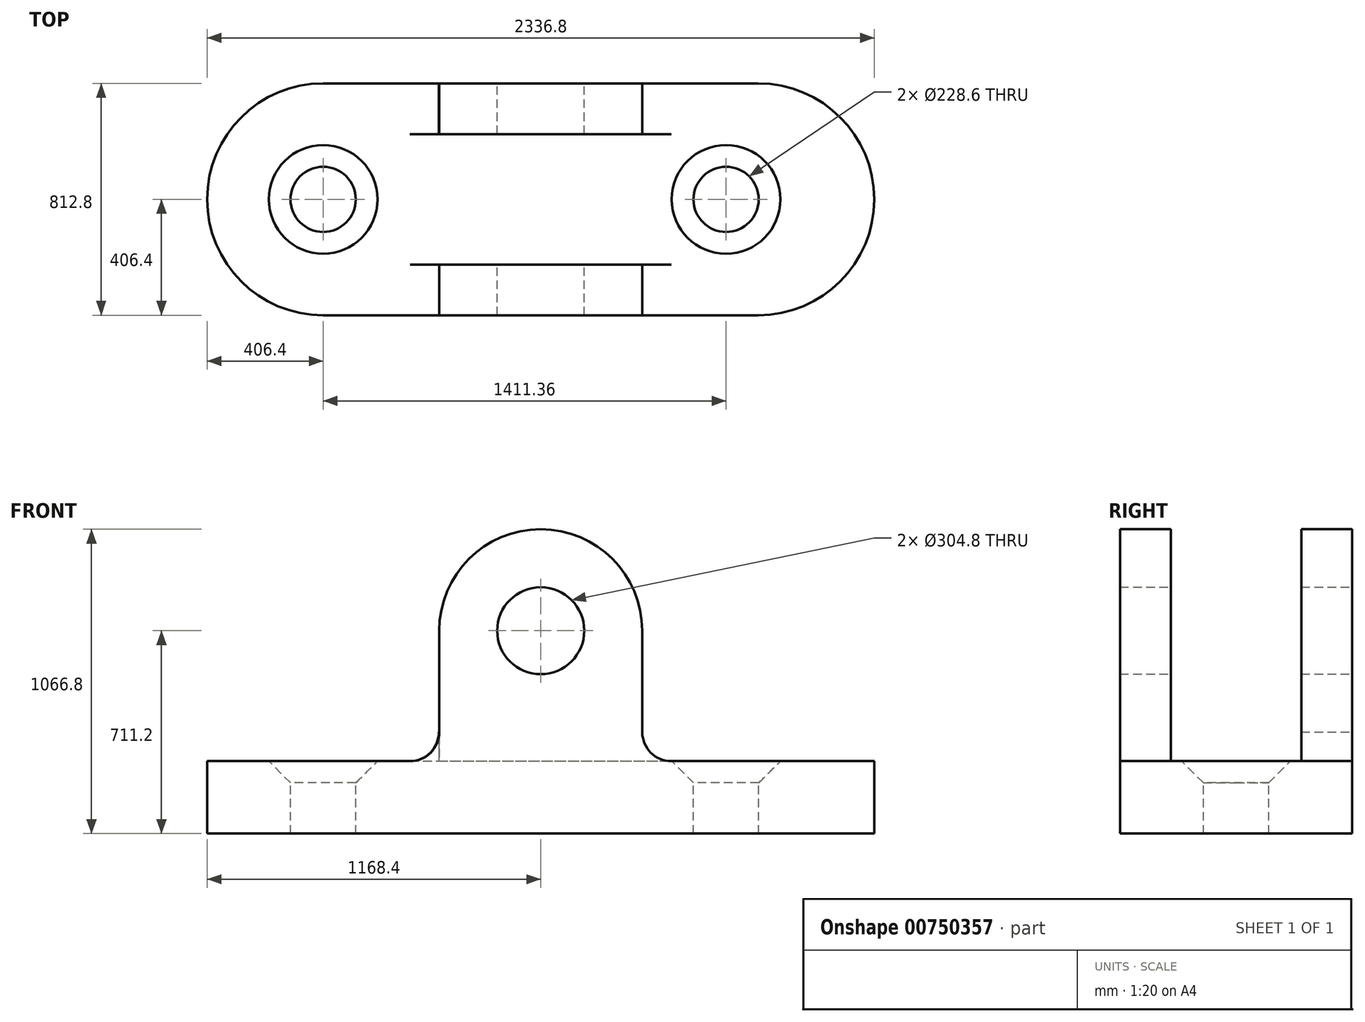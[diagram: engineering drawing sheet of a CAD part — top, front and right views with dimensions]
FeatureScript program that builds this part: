
annotation { "Feature Type Name" : "Feature", "Feature Type Description" : "" }
export const myFeature = defineFeature(function(context is Context, id is Id, definition is map)
    precondition{}
    {
        {
            var Q0;
            Q0=qCreatedBy(makeId("Top.planeOp"),FACE);
            var sketch = newSketch(context, id + "F0", { "sketchPlane" : qUnion([Q0])});
            skLineSegment(sketch, "E0.bottom", {"start": v(-762, -406.4) * mm, "end": v(762, -406.4) * mm});
            skLineSegment(sketch, "E0.top", {"start": v(-762, 406.4) * mm, "end": v(762, 406.4) * mm});
            skPoint(sketch, "E0.middle", {"position": v(0, 0) * mm});
            skArc(sketch, "E1", {"start": v(-762, 406.4) * mm, "mid": v(-1168.4, 0) * mm, "end": v(-762, -406.4) * mm});
            skArc(sketch, "E2", {"start": v(762, -406.4) * mm, "mid": v(1168.4, 0) * mm, "end": v(762, 406.4) * mm});
            skPoint(sketch, "E3.orphan", {"position": v(1168.4, 406.4) * mm});
            skPoint(sketch, "E4.orphan", {"position": v(1168.4, -406.4) * mm});
            skPoint(sketch, "E5.orphan", {"position": v(-1168.4, -406.4) * mm});
            skPoint(sketch, "E6.orphan", {"position": v(-1168.4, 406.4) * mm});
            skPoint(sketch, "E7.orphan", {"position": v(1168.4, 0) * mm});
            skPoint(sketch, "E8.start.orphan", {"position": v(-1168.4, 0) * mm});
            skSolve(sketch);
        }
        {
            var Q0;
            Q0=makeQuery(id+"F0.imprint","IMPRINT",FACE,{"disambiguationData":[TD([[makeQuery(id+"F0.imprint","IMPRINT",EDGE,{"derivedFrom":sQuery(id+"F0.wireOp",EDGE,"E0.bottom")}),1.0]])]});
            extrude(context, id + "F1", {"entities" : qUnion([Q0]), "endBound" : BoundingType.SYMMETRIC, "depth" : 254 * mm, "offsetDistance" : 25.4 * mm});
        }
        {
            var Q0;
            Q0=makeQuery(id+"F1.opExtrude","CAP_FACE",FACE,{"disambiguationData":[OSD([sQuery(id+"F0.wireOp",EDGE,"E0.bottom"),sQuery(id+"F0.wireOp",EDGE,"E0.top"),sQuery(id+"F0.wireOp",EDGE,"E1"),sQuery(id+"F0.wireOp",EDGE,"E2")])],"isStart":false});
            var sketch = newSketch(context, id + "F2", { "sketchPlane" : qUnion([Q0])});
            skLineSegment(sketch, "E9", {"start": v(-355.6, 228.6) * mm, "end": v(355.6, 228.6) * mm});
            skLineSegment(sketch, "E10", {"start": v(-355.6, -228.6) * mm, "end": v(355.6, -228.6) * mm});
            skLineSegment(sketch, "E11", {"start": v(355.6, 406.4) * mm, "end": v(355.6, 228.6) * mm});
            skLineSegment(sketch, "E12", {"start": v(-355.6, 406.4) * mm, "end": v(-355.6, 228.6) * mm});
            skPoint(sketch, "E13.orphan", {"position": v(0, 406.4) * mm});
            skPoint(sketch, "E14.orphan", {"position": v(0, -406.4) * mm});
            skLineSegment(sketch, "E15.trimOffspring", {"start": v(-355.6, -228.6) * mm, "end": v(-355.6, -406.4) * mm});
            skLineSegment(sketch, "E16.trimOffspring", {"start": v(355.6, -228.6) * mm, "end": v(355.6, -406.4) * mm});
            skCircle(sketch, "E17", {"center": v(-762, 0) * mm, "radius": 114.3 * mm});
            skCircle(sketch, "E18", {"center": v(649.36, 0) * mm, "radius": 114.3 * mm});
            skSolve(sketch);
        }
        {
            var Q0;
            Q0=makeQuery(id+"F2.imprint","IMPRINT",FACE,{"disambiguationData":[TD([[makeQuery(id+"F2.imprint","IMPRINT",EDGE,{"derivedFrom":sQuery(id+"F2.wireOp",EDGE,"E10")}),-1.0]])]});
            var Q1;
            Q1=makeQuery(id+"F2.imprint","IMPRINT",FACE,{"disambiguationData":[TD([[makeQuery(id+"F2.imprint","IMPRINT",EDGE,{"derivedFrom":sQuery(id+"F2.wireOp",EDGE,"E9")}),1.0]])]});
            extrude(context, id + "F3", {"entities" : qUnion([Q0, Q1]), "operationType" : NewBodyOperationType.ADD, "depth" : 812.8 * mm, "offsetDistance" : 25.4 * mm});
        }
        {
            var Q0;
            Q0=sQuery(id+"F2.wireOp",VERTEX,"E18.center");
            var Q1;
            Q1=sQuery(id+"F2.wireOp",VERTEX,"E17.center");
            var Q2;
            Q2=makeQuery(id+"F1.opExtrude","SWEPT_BODY",BODY,{"disambiguationData":[OSD([sQuery(id+"F0.wireOp",EDGE,"E0.bottom"),sQuery(id+"F0.wireOp",EDGE,"E0.top"),sQuery(id+"F0.wireOp",EDGE,"E1"),sQuery(id+"F0.wireOp",EDGE,"E2")])]});
            hole(context, id + "F4", {"style" : HoleStyle.C_SINK, "endStyle" : HoleEndStyle.THROUGH, "holeDiameter" : 228.6 * mm, "cSinkDiameter" : 381 * mm, "cSinkAngle" : 90 * degree, "majorDiameter" : 6.35 * mm, "isTappedThrough" : true, "tappedDepth" : 12.7 * mm, "tapClearance" : 3, "locations" : qUnion([Q0, Q1]), "scope" : qUnion([Q2])});
        }
        {
            var Q0;
            {var subQ0=sQuery(id+"F0.wireOp",EDGE,"E0.bottom");Q0=makeQuery(id+"F3.boolean.opBoolean","MERGE",FACE,{"derivedFrom":[makeQuery(id+"F1.opExtrude","SWEPT_FACE",FACE,{"disambiguationData":[OSD([subQ0])]}),makeQuery(id+"F3.opExtrude","SWEPT_FACE",FACE,{"disambiguationData":[OSD([subQ0])]})]});}
            var sketch = newSketch(context, id + "F5", { "sketchPlane" : qUnion([Q0])});
            skLineSegment(sketch, "E19", {"start": v(-355.6, 584.2) * mm, "end": v(355.6, 584.2) * mm});
            skArc(sketch, "E20", {"start": v(355.6, 584.2) * mm, "mid": v(0, 939.8) * mm, "end": v(-355.6, 584.2) * mm});
            skPoint(sketch, "E21.end.orphan", {"position": v(0, 939.8) * mm});
            skLineSegment(sketch, "E22", {"start": v(355.6, 584.2) * mm, "end": v(-355.6, 584.2) * mm});
            skSolve(sketch);
        }
        {
            var Q0;
            {var subQ0=sQuery(id+"F0.wireOp",EDGE,"E0.top");Q0=makeQuery(id+"F3.boolean.opBoolean","MERGE",FACE,{"derivedFrom":[makeQuery(id+"F1.opExtrude","SWEPT_FACE",FACE,{"disambiguationData":[OSD([subQ0])]}),makeQuery(id+"F3.opExtrude","SWEPT_FACE",FACE,{"disambiguationData":[OSD([subQ0])]})]});}
            var sketch = newSketch(context, id + "F6", { "sketchPlane" : qUnion([Q0])});
            skLineSegment(sketch, "E23", {"start": v(-355.6, 584.2) * mm, "end": v(355.6, 584.2) * mm});
            skArc(sketch, "E24", {"start": v(355.6, 584.2) * mm, "mid": v(0, 939.8) * mm, "end": v(-355.6, 584.2) * mm});
            skSolve(sketch);
        }
        {
            var Q0;
            {var subQ0=sQuery(id+"F5.wireOp",EDGE,"E20");var subQ1=sQuery(id+"F0.wireOp",EDGE,"E0.bottom");var subQ4=makeQuery(id+"F3.opExtrude","CAP_EDGE",EDGE,{"disambiguationData":[OSD([subQ1])],"isStart":false});var subQ5=makeQuery(id+"F5.imprint","INTERSECT",VERTEX,{"derivedFrom":[subQ4,subQ0]});Q0=makeQuery(id+"F5.imprint","IMPRINT",FACE,{"disambiguationData":[TD([[makeQuery(id+"F5.imprint","IMPRINT",EDGE,{"disambiguationData":[TD([[subQ5,1.0]])],"derivedFrom":subQ4}),-1.0]])]});}
            var Q1;
            {var subQ0=sQuery(id+"F5.wireOp",EDGE,"E20");var subQ1=sQuery(id+"F0.wireOp",EDGE,"E0.bottom");var subQ4=makeQuery(id+"F3.opExtrude","CAP_EDGE",EDGE,{"disambiguationData":[OSD([subQ1])],"isStart":false});var subQ5=makeQuery(id+"F5.imprint","INTERSECT",VERTEX,{"derivedFrom":[subQ4,subQ0]});Q1=makeQuery(id+"F5.imprint","IMPRINT",FACE,{"disambiguationData":[TD([[makeQuery(id+"F5.imprint","IMPRINT",EDGE,{"disambiguationData":[TD([[subQ5,-1.0]])],"derivedFrom":subQ4}),-1.0]])]});}
            extrude(context, id + "F7", {"entities" : qUnion([Q0, Q1]), "operationType" : NewBodyOperationType.REMOVE, "oppositeDirection" : true, "depth" : 177.8 * mm, "offsetDistance" : 25.4 * mm});
        }
        {
            var Q0;
            {var subQ0=sQuery(id+"F6.wireOp",EDGE,"E24");var subQ1=sQuery(id+"F0.wireOp",EDGE,"E0.top");var subQ4=makeQuery(id+"F3.opExtrude","CAP_EDGE",EDGE,{"disambiguationData":[OSD([subQ1])],"isStart":false});var subQ5=makeQuery(id+"F6.imprint","INTERSECT",VERTEX,{"derivedFrom":[subQ4,subQ0]});Q0=makeQuery(id+"F6.imprint","IMPRINT",FACE,{"disambiguationData":[TD([[makeQuery(id+"F6.imprint","IMPRINT",EDGE,{"disambiguationData":[TD([[subQ5,-1.0]])],"derivedFrom":subQ4}),1.0]])]});}
            var Q1;
            {var subQ0=sQuery(id+"F6.wireOp",EDGE,"E24");var subQ1=sQuery(id+"F0.wireOp",EDGE,"E0.top");var subQ4=makeQuery(id+"F3.opExtrude","CAP_EDGE",EDGE,{"disambiguationData":[OSD([subQ1])],"isStart":false});var subQ5=makeQuery(id+"F6.imprint","INTERSECT",VERTEX,{"derivedFrom":[subQ4,subQ0]});Q1=makeQuery(id+"F6.imprint","IMPRINT",FACE,{"disambiguationData":[TD([[makeQuery(id+"F6.imprint","IMPRINT",EDGE,{"disambiguationData":[TD([[subQ5,1.0]])],"derivedFrom":subQ4}),1.0]])]});}
            extrude(context, id + "F8", {"entities" : qUnion([Q0, Q1]), "operationType" : NewBodyOperationType.REMOVE, "oppositeDirection" : true, "depth" : 177.8 * mm, "offsetDistance" : 25.4 * mm});
        }
        {
            var Q0;
            Q0=sQuery(id+"F6.wireOp",VERTEX,"E24.center");
            var Q1;
            Q1=makeQuery(id+"F1.opExtrude","SWEPT_BODY",BODY,{"disambiguationData":[OSD([sQuery(id+"F0.wireOp",EDGE,"E0.bottom"),sQuery(id+"F0.wireOp",EDGE,"E0.top"),sQuery(id+"F0.wireOp",EDGE,"E1"),sQuery(id+"F0.wireOp",EDGE,"E2")])]});
            hole(context, id + "F9", {"style" : HoleStyle.SIMPLE, "endStyle" : HoleEndStyle.THROUGH, "holeDiameter" : 304.8 * mm, "majorDiameter" : 6.35 * mm, "isTappedThrough" : true, "tappedDepth" : 12.7 * mm, "tapClearance" : 3, "locations" : qUnion([Q0]), "scope" : qUnion([Q1])});
        }
        {
            var Q0;
            {var subQ0=sQuery(id+"F0.wireOp",EDGE,"E0.bottom");Q0=makeQuery(id+"F3.boolean.opBoolean","MERGE",FACE,{"derivedFrom":[makeQuery(id+"F1.opExtrude","SWEPT_FACE",FACE,{"disambiguationData":[OSD([subQ0])]}),makeQuery(id+"F3.opExtrude","SWEPT_FACE",FACE,{"disambiguationData":[OSD([subQ0])]})]});}
            var sketch = newSketch(context, id + "F10", { "sketchPlane" : qUnion([Q0])});
            skLineSegment(sketch, "E25", {"start": v(-355.6, 127) * mm, "end": v(-457.2, 127) * mm});
            skLineSegment(sketch, "E26", {"start": v(-457.2, 127) * mm, "end": v(-457.2, 228.6) * mm});
            skLineSegment(sketch, "E27", {"start": v(-457.2, 228.6) * mm, "end": v(-355.6, 228.6) * mm});
            skLineSegment(sketch, "E28", {"start": v(-355.6, 228.6) * mm, "end": v(-355.6, 127) * mm});
            skLineSegment(sketch, "E29", {"start": v(355.6, 127) * mm, "end": v(457.2, 127) * mm});
            skLineSegment(sketch, "E30", {"start": v(457.2, 127) * mm, "end": v(457.2, 228.6) * mm});
            skLineSegment(sketch, "E31", {"start": v(457.2, 228.6) * mm, "end": v(355.6, 228.6) * mm});
            skLineSegment(sketch, "E32", {"start": v(355.6, 228.6) * mm, "end": v(355.6, 127) * mm});
            skCircle(sketch, "E33", {"center": v(-457.2, 228.6) * mm, "radius": 101.6 * mm});
            skCircle(sketch, "E34", {"center": v(457.2, 228.6) * mm, "radius": 101.6 * mm});
            skSolve(sketch);
        }
        {
            var Q0;
            {var subQ0=sQuery(id+"F10.wireOp",EDGE,"E25");Q0=makeQuery(id+"F10.imprint","IMPRINT",FACE,{"disambiguationData":[TD([[makeQuery(id+"F10.imprint","IMPRINT",EDGE,{"derivedFrom":subQ0}),1.0]])]});}
            var Q1;
            {var subQ0=sQuery(id+"F10.wireOp",EDGE,"E29");Q1=makeQuery(id+"F10.imprint","IMPRINT",FACE,{"disambiguationData":[TD([[makeQuery(id+"F10.imprint","IMPRINT",EDGE,{"derivedFrom":subQ0}),1.0]])]});}
            extrude(context, id + "F11", {"entities" : qUnion([Q0, Q1]), "operationType" : NewBodyOperationType.ADD, "depth" : -177.8 * mm, "offsetDistance" : 25.4 * mm});
        }
        {
            var Q0;
            {var subQ3=sQuery(id+"F6.wireOp",EDGE,"E23");Q0=makeQuery(id+"F6.imprint","IMPRINT",FACE,{"disambiguationData":[TD([[makeQuery(id+"F6.imprint","IMPRINT",EDGE,{"derivedFrom":subQ3}),-1.0]])]});}
            var sketch = newSketch(context, id + "F12", { "sketchPlane" : qUnion([Q0])});
            skLineSegment(sketch, "E35", {"start": v(0, 0) * mm, "end": v(0, 228.6) * mm});
            skLineSegment(sketch, "E36", {"start": v(0, 228.6) * mm, "end": v(-355.6, 228.6) * mm});
            skLineSegment(sketch, "E37", {"start": v(-355.6, 228.6) * mm, "end": v(-457.2, 228.6) * mm});
            skLineSegment(sketch, "E38", {"start": v(-457.2, 228.6) * mm, "end": v(-457.2, 127) * mm});
            skLineSegment(sketch, "E39", {"start": v(-457.2, 127) * mm, "end": v(-355.6, 127) * mm});
            skLineSegment(sketch, "E40", {"start": v(-355.6, 127) * mm, "end": v(-355.6, 228.6) * mm});
            skCircle(sketch, "E41", {"center": v(-457.2, 228.6) * mm, "radius": 101.6 * mm});
            skLineSegment(sketch, "E42", {"start": v(0, 228.6) * mm, "end": v(356.83, 228.6) * mm});
            skLineSegment(sketch, "E43", {"start": v(356.83, 228.6) * mm, "end": v(356.83, 127) * mm});
            skLineSegment(sketch, "E44", {"start": v(356.83, 127) * mm, "end": v(458.43, 127) * mm});
            skLineSegment(sketch, "E45", {"start": v(458.43, 127) * mm, "end": v(458.43, 228.6) * mm});
            skLineSegment(sketch, "E46", {"start": v(458.43, 228.6) * mm, "end": v(356.83, 228.6) * mm});
            skCircle(sketch, "E47", {"center": v(458.43, 228.6) * mm, "radius": 101.6 * mm});
            skSolve(sketch);
        }
        {
            var Q0;
            {var subQ0=sQuery(id+"F12.wireOp",EDGE,"E39");Q0=makeQuery(id+"F12.imprint","IMPRINT",FACE,{"disambiguationData":[TD([[makeQuery(id+"F12.imprint","IMPRINT",EDGE,{"derivedFrom":subQ0}),-1.0]])]});}
            var Q1;
            {var subQ0=sQuery(id+"F12.wireOp",EDGE,"E43");Q1=makeQuery(id+"F12.imprint","IMPRINT",FACE,{"disambiguationData":[TD([[makeQuery(id+"F12.imprint","IMPRINT",EDGE,{"derivedFrom":subQ0}),1.0]])]});}
            extrude(context, id + "F13", {"entities" : qUnion([Q0, Q1]), "operationType" : NewBodyOperationType.ADD, "depth" : -177.8 * mm, "offsetDistance" : 25.4 * mm});
        }
    });
